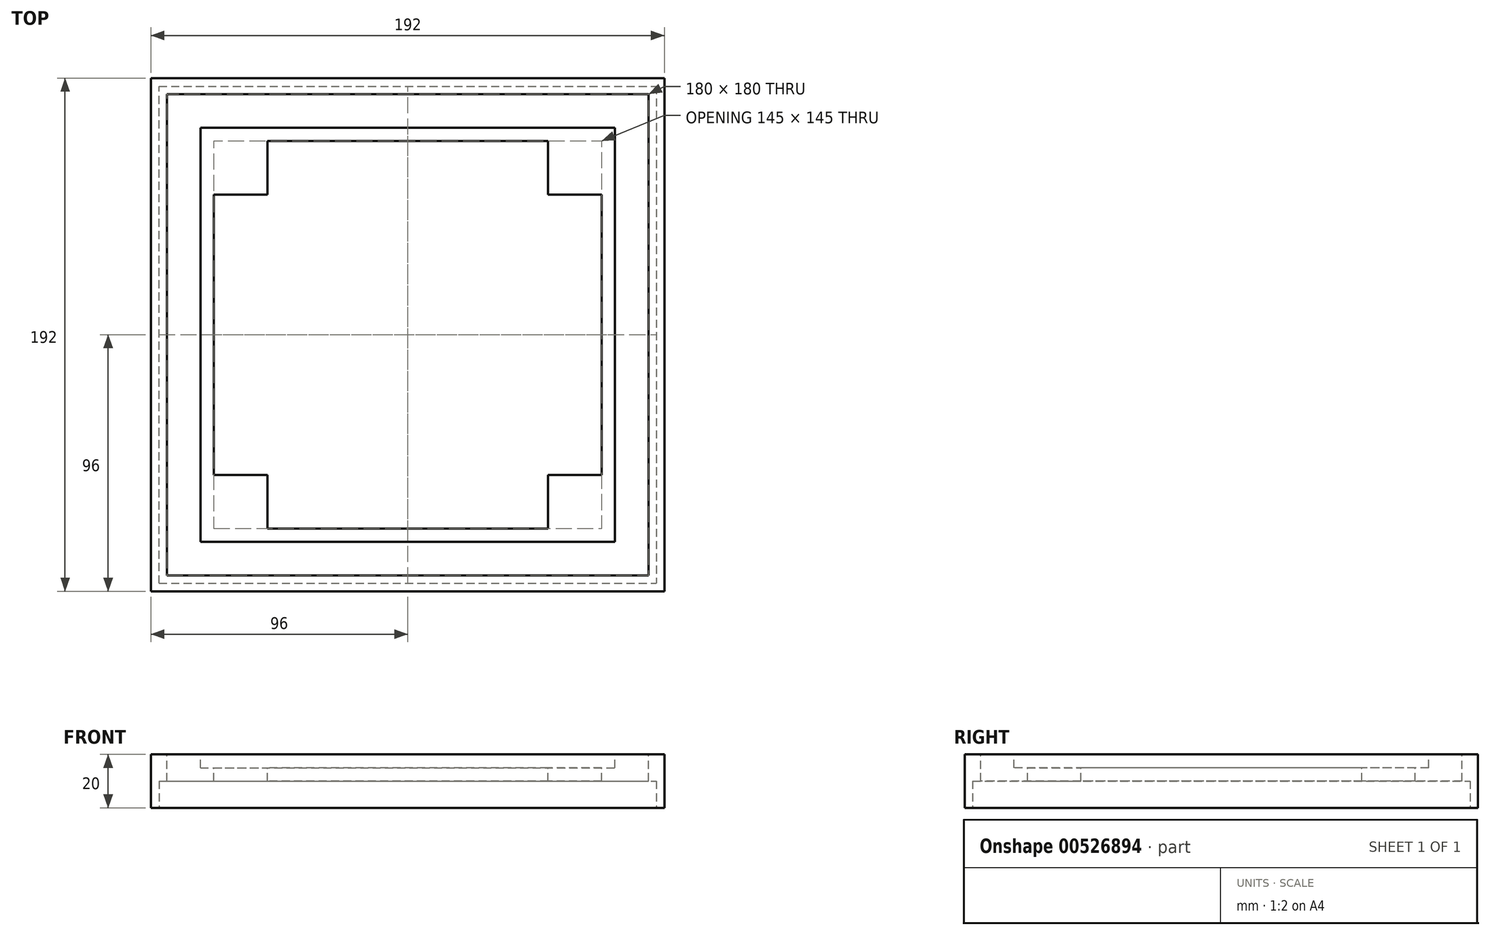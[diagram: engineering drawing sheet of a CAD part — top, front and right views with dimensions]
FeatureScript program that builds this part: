
annotation { "Feature Type Name" : "Feature", "Feature Type Description" : "" }
export const myFeature = defineFeature(function(context is Context, id is Id, definition is map)
    precondition{}
    {
        {
            var Q0;
            Q0=qCreatedBy(makeId("Top.planeOp"),FACE);
            var sketch = newSketch(context, id + "F0", { "sketchPlane" : qUnion([Q0])});
            skLineSegment(sketch, "E0.bottom", {"start": v(90, -90) * mm, "end": v(-90, -90) * mm});
            skLineSegment(sketch, "E0.top", {"start": v(90, 90) * mm, "end": v(-90, 90) * mm});
            skLineSegment(sketch, "E0.left", {"start": v(90, -90) * mm, "end": v(90, 90) * mm});
            skLineSegment(sketch, "E0.right", {"start": v(-90, -90) * mm, "end": v(-90, 90) * mm});
            skPoint(sketch, "E0.middle", {"position": v(0, 0) * mm});
            skSolve(sketch);
        }
        {
            var Q0;
            Q0=makeQuery(id+"F0.imprint","IMPRINT",FACE,{"disambiguationData":[TD([[makeQuery(id+"F0.imprint","IMPRINT",EDGE,{"derivedFrom":sQuery(id+"F0.wireOp",EDGE,"E0.bottom")}),-1.0]])]});
            extrude(context, id + "F1", {"entities" : qUnion([Q0]), "depth" : 70 * mm, "offsetDistance" : 25 * mm});
        }
        {
            var Q0;
            Q0=makeQuery(id+"F1.opExtrude","CAP_FACE",FACE,{"disambiguationData":[OSD([sQuery(id+"F0.wireOp",EDGE,"E0.bottom"),sQuery(id+"F0.wireOp",EDGE,"E0.top"),sQuery(id+"F0.wireOp",EDGE,"E0.left"),sQuery(id+"F0.wireOp",EDGE,"E0.right")])],"isStart":false});
            shell(context, id + "F2", {"entities" : qUnion([Q0]), "thickness" : 5 * mm});
        }
        {
            var Q0;
            Q0=makeQuery(id+"F1.opExtrude","CAP_FACE",FACE,{"disambiguationData":[OSD([sQuery(id+"F0.wireOp",EDGE,"E0.bottom"),sQuery(id+"F0.wireOp",EDGE,"E0.top"),sQuery(id+"F0.wireOp",EDGE,"E0.left"),sQuery(id+"F0.wireOp",EDGE,"E0.right")])],"isStart":false});
            var sketch = newSketch(context, id + "F3", { "sketchPlane" : qUnion([Q0])});
            skLineSegment(sketch, "E1.bottom", {"start": v(-85, 85) * mm, "end": v(85, 85) * mm});
            skLineSegment(sketch, "E1.top", {"start": v(-85, -85) * mm, "end": v(85, -85) * mm});
            skLineSegment(sketch, "E1.left", {"start": v(-85, 85) * mm, "end": v(-85, -85) * mm});
            skLineSegment(sketch, "E1.right", {"start": v(85, 85) * mm, "end": v(85, -85) * mm});
            skPoint(sketch, "E1.middle", {"position": v(0, 0) * mm});
            skSolve(sketch);
        }
        {
            var Q0;
            Q0=qSketchRegion(id+"F3",true);
            extrude(context, id + "F4", {"entities" : qUnion([Q0]), "operationType" : NewBodyOperationType.ADD, "oppositeDirection" : true, "depth" : 10 * mm, "offsetDistance" : 25 * mm});
        }
        {
            var Q0;
            Q0=makeQuery(id+"F4.boolean.opBoolean","MERGE",FACE,{"derivedFrom":[makeQuery(id+"F1.opExtrude","CAP_FACE",FACE,{"disambiguationData":[OSD([sQuery(id+"F0.wireOp",EDGE,"E0.bottom"),sQuery(id+"F0.wireOp",EDGE,"E0.top"),sQuery(id+"F0.wireOp",EDGE,"E0.left"),sQuery(id+"F0.wireOp",EDGE,"E0.right")])],"isStart":false}),makeQuery(id+"F4.opExtrude","CAP_FACE",FACE,{"disambiguationData":[OSD([sQuery(id+"F3.wireOp",EDGE,"E1.bottom"),sQuery(id+"F3.wireOp",EDGE,"E1.top"),sQuery(id+"F3.wireOp",EDGE,"E1.left"),sQuery(id+"F3.wireOp",EDGE,"E1.right")])],"isStart":true})]});
            var sketch = newSketch(context, id + "F5", { "sketchPlane" : qUnion([Q0])});
            skLineSegment(sketch, "E2.bottom", {"start": v(-77.5, 77.5) * mm, "end": v(77.5, 77.5) * mm});
            skLineSegment(sketch, "E2.top", {"start": v(-77.5, -77.5) * mm, "end": v(77.5, -77.5) * mm});
            skLineSegment(sketch, "E2.left", {"start": v(-77.5, 77.5) * mm, "end": v(-77.5, -77.5) * mm});
            skLineSegment(sketch, "E2.right", {"start": v(77.5, 77.5) * mm, "end": v(77.5, -77.5) * mm});
            skPoint(sketch, "E2.middle", {"position": v(0, 0) * mm});
            skSolve(sketch);
        }
        {
            var Q0;
            Q0=qSketchRegion(id+"F5",true);
            var Q1;
            Q1=makeQuery(id+"F5.imprint","IMPRINT",FACE,{"disambiguationData":[TD([[makeQuery(id+"F5.imprint","IMPRINT",EDGE,{"derivedFrom":sQuery(id+"F5.wireOp",EDGE,"E2.bottom")}),-1.0]])]});
            extrude(context, id + "F6", {"entities" : qUnion([Q0, Q1]), "operationType" : NewBodyOperationType.REMOVE, "oppositeDirection" : true, "depth" : 5 * mm, "offsetDistance" : 25 * mm});
        }
        {
            var Q0;
            Q0=makeQuery(id+"F6.boolean.opBoolean","COPY",FACE,{"derivedFrom":makeQuery(id+"F6.opExtrude","CAP_FACE",FACE,{"disambiguationData":[OSD([sQuery(id+"F5.wireOp",EDGE,"E2.bottom"),sQuery(id+"F5.wireOp",EDGE,"E2.top"),sQuery(id+"F5.wireOp",EDGE,"E2.left"),sQuery(id+"F5.wireOp",EDGE,"E2.right")])],"isStart":false})});
            var sketch = newSketch(context, id + "F7", { "sketchPlane" : qUnion([Q0])});
            skLineSegment(sketch, "E3.bottom", {"start": v(72.5, 72.5) * mm, "end": v(-72.5, 72.5) * mm});
            skLineSegment(sketch, "E3.top", {"start": v(72.5, -72.5) * mm, "end": v(-72.5, -72.5) * mm});
            skLineSegment(sketch, "E3.left", {"start": v(72.5, 72.5) * mm, "end": v(72.5, -72.5) * mm});
            skLineSegment(sketch, "E3.right", {"start": v(-72.5, 72.5) * mm, "end": v(-72.5, -72.5) * mm});
            skPoint(sketch, "E3.middle", {"position": v(0, 0) * mm});
            skSolve(sketch);
        }
        {
            var Q0;
            Q0=makeQuery(id+"F7.imprint","IMPRINT",FACE,{"disambiguationData":[TD([[makeQuery(id+"F7.imprint","IMPRINT",EDGE,{"derivedFrom":sQuery(id+"F7.wireOp",EDGE,"E3.bottom")}),1.0]])]});
            extrude(context, id + "F8", {"entities" : qUnion([Q0]), "operationType" : NewBodyOperationType.REMOVE, "oppositeDirection" : true, "depth" : 25 * mm, "offsetDistance" : 25 * mm});
        }
        {
            var Q0;
            Q0=makeQuery(id+"F6.boolean.opBoolean","COPY",FACE,{"derivedFrom":makeQuery(id+"F6.opExtrude","CAP_FACE",FACE,{"disambiguationData":[OSD([sQuery(id+"F5.wireOp",EDGE,"E2.bottom"),sQuery(id+"F5.wireOp",EDGE,"E2.top"),sQuery(id+"F5.wireOp",EDGE,"E2.left"),sQuery(id+"F5.wireOp",EDGE,"E2.right")])],"isStart":false})});
            var sketch = newSketch(context, id + "F9", { "sketchPlane" : qUnion([Q0])});
            skLineSegment(sketch, "E4.bottom", {"start": v(-72.5, 72.5) * mm, "end": v(-52.5, 72.5) * mm});
            skLineSegment(sketch, "E4.top", {"start": v(-72.5, 52.5) * mm, "end": v(-52.5, 52.5) * mm});
            skLineSegment(sketch, "E4.left", {"start": v(-72.5, 72.5) * mm, "end": v(-72.5, 52.5) * mm});
            skLineSegment(sketch, "E4.right", {"start": v(-52.5, 72.5) * mm, "end": v(-52.5, 52.5) * mm});
            skLineSegment(sketch, "E5.bottom", {"start": v(72.5, 72.5) * mm, "end": v(52.5, 72.5) * mm});
            skLineSegment(sketch, "E5.top", {"start": v(72.5, 52.5) * mm, "end": v(52.5, 52.5) * mm});
            skLineSegment(sketch, "E5.left", {"start": v(72.5, 72.5) * mm, "end": v(72.5, 52.5) * mm});
            skLineSegment(sketch, "E5.right", {"start": v(52.5, 72.5) * mm, "end": v(52.5, 52.5) * mm});
            skLineSegment(sketch, "E6.bottom", {"start": v(72.5, -72.5) * mm, "end": v(52.5, -72.5) * mm});
            skLineSegment(sketch, "E6.top", {"start": v(72.5, -52.5) * mm, "end": v(52.5, -52.5) * mm});
            skLineSegment(sketch, "E6.left", {"start": v(72.5, -72.5) * mm, "end": v(72.5, -52.5) * mm});
            skLineSegment(sketch, "E6.right", {"start": v(52.5, -72.5) * mm, "end": v(52.5, -52.5) * mm});
            skLineSegment(sketch, "E7.bottom", {"start": v(-72.5, -72.5) * mm, "end": v(-52.5, -72.5) * mm});
            skLineSegment(sketch, "E7.top", {"start": v(-72.5, -52.5) * mm, "end": v(-52.5, -52.5) * mm});
            skLineSegment(sketch, "E7.left", {"start": v(-72.5, -72.5) * mm, "end": v(-72.5, -52.5) * mm});
            skLineSegment(sketch, "E7.right", {"start": v(-52.5, -72.5) * mm, "end": v(-52.5, -52.5) * mm});
            skSolve(sketch);
        }
        {
            var Q0;
            Q0=makeQuery(id+"F9.imprint","IMPRINT",FACE,{"disambiguationData":[TD([[makeQuery(id+"F9.imprint","IMPRINT",EDGE,{"derivedFrom":sQuery(id+"F9.wireOp",EDGE,"E4.bottom")}),1.0]])]});
            var Q1;
            Q1=makeQuery(id+"F9.imprint","IMPRINT",FACE,{"disambiguationData":[TD([[makeQuery(id+"F9.imprint","IMPRINT",EDGE,{"derivedFrom":sQuery(id+"F9.wireOp",EDGE,"E5.bottom")}),1.0]])]});
            var Q2;
            Q2=makeQuery(id+"F9.imprint","IMPRINT",FACE,{"disambiguationData":[TD([[makeQuery(id+"F9.imprint","IMPRINT",EDGE,{"derivedFrom":sQuery(id+"F9.wireOp",EDGE,"E6.bottom")}),-1.0]])]});
            var Q3;
            Q3=makeQuery(id+"F9.imprint","IMPRINT",FACE,{"disambiguationData":[TD([[makeQuery(id+"F9.imprint","IMPRINT",EDGE,{"derivedFrom":sQuery(id+"F9.wireOp",EDGE,"E7.bottom")}),-1.0]])]});
            extrude(context, id + "F10", {"entities" : qUnion([Q0, Q1, Q2, Q3]), "operationType" : NewBodyOperationType.ADD, "oppositeDirection" : true, "depth" : 5 * mm, "offsetDistance" : 25 * mm});
        }
        {
            var Q0;
            Q0=makeQuery(id+"F1.opExtrude","CAP_FACE",FACE,{"disambiguationData":[OSD([sQuery(id+"F0.wireOp",EDGE,"E0.bottom"),sQuery(id+"F0.wireOp",EDGE,"E0.top"),sQuery(id+"F0.wireOp",EDGE,"E0.left"),sQuery(id+"F0.wireOp",EDGE,"E0.right")])],"isStart":true});
            var sketch = newSketch(context, id + "F11", { "sketchPlane" : qUnion([Q0])});
            skLineSegment(sketch, "E8.bottom", {"start": v(130.66, 148.52) * mm, "end": v(-106.26, 148.52) * mm});
            skLineSegment(sketch, "E8.top", {"start": v(130.66, -115.94) * mm, "end": v(-106.26, -115.94) * mm});
            skLineSegment(sketch, "E8.left", {"start": v(130.66, 148.52) * mm, "end": v(130.66, -115.94) * mm});
            skLineSegment(sketch, "E8.right", {"start": v(-106.26, 148.52) * mm, "end": v(-106.26, -115.94) * mm});
            skSolve(sketch);
        }
        {
            var Q0;
            Q0=makeQuery(id+"F11.imprint","IMPRINT",FACE,{"disambiguationData":[TD([[makeQuery(id+"F11.imprint","IMPRINT",EDGE,{"derivedFrom":sQuery(id+"F11.wireOp",EDGE,"E8.bottom")}),1.0]])]});
            extrude(context, id + "F12", {"entities" : qUnion([Q0]), "operationType" : NewBodyOperationType.REMOVE, "oppositeDirection" : true, "depth" : 25 * mm, "offsetDistance" : 25 * mm});
        }
        {
            var Q0;
            Q0=makeQuery(id+"F1.opExtrude","CAP_FACE",FACE,{"disambiguationData":[OSD([sQuery(id+"F0.wireOp",EDGE,"E0.bottom"),sQuery(id+"F0.wireOp",EDGE,"E0.top"),sQuery(id+"F0.wireOp",EDGE,"E0.left"),sQuery(id+"F0.wireOp",EDGE,"E0.right")])],"isStart":true});
            var sketch = newSketch(context, id + "F13", { "sketchPlane" : qUnion([Q0])});
            skLineSegment(sketch, "E9.bottom", {"start": v(99.38, 138.7) * mm, "end": v(-144.6, 138.7) * mm});
            skLineSegment(sketch, "E9.top", {"start": v(99.38, -180.9) * mm, "end": v(-144.6, -180.9) * mm});
            skLineSegment(sketch, "E9.left", {"start": v(99.38, 138.7) * mm, "end": v(99.38, -180.9) * mm});
            skLineSegment(sketch, "E9.right", {"start": v(-144.6, 138.7) * mm, "end": v(-144.6, -180.9) * mm});
            skSolve(sketch);
        }
        {
            var Q0;
            Q0=makeQuery(id+"F13.imprint","IMPRINT",FACE,{"disambiguationData":[TD([[makeQuery(id+"F13.imprint","IMPRINT",EDGE,{"derivedFrom":sQuery(id+"F13.wireOp",EDGE,"E9.bottom")}),1.0]])]});
            var Q1;
            Q1=makeQuery(id+"F13.imprint","IMPRINT",FACE,{"disambiguationData":[TD([[makeQuery(id+"F13.imprint","IMPRINT",EDGE,{"derivedFrom":makeQuery(id+"F1.opExtrude","CAP_EDGE",EDGE,{"disambiguationData":[OSD([sQuery(id+"F0.wireOp",EDGE,"E0.bottom")])],"isStart":true})}),1.0]])]});
            extrude(context, id + "F14", {"entities" : qUnion([Q0, Q1]), "operationType" : NewBodyOperationType.REMOVE, "oppositeDirection" : true, "depth" : 55 * mm, "offsetDistance" : 25 * mm, "hasSecondDirection" : true, "secondDirectionOppositeDirection" : false, "secondDirectionDepth" : 25 * mm});
        }
        {
            var Q0;
            Q0=makeQuery(id+"F10.boolean.opBoolean","MERGE",FACE,{"derivedFrom":[makeQuery(id+"F4.opExtrude","CAP_FACE",FACE,{"disambiguationData":[OSD([sQuery(id+"F3.wireOp",EDGE,"E1.bottom"),sQuery(id+"F3.wireOp",EDGE,"E1.top"),sQuery(id+"F3.wireOp",EDGE,"E1.left"),sQuery(id+"F3.wireOp",EDGE,"E1.right")])],"isStart":false}),makeQuery(id+"F10.opExtrude","CAP_FACE",FACE,{"disambiguationData":[OSD([sQuery(id+"F9.wireOp",EDGE,"E4.bottom"),sQuery(id+"F9.wireOp",EDGE,"E4.top"),sQuery(id+"F9.wireOp",EDGE,"E4.left"),sQuery(id+"F9.wireOp",EDGE,"E4.right")])],"isStart":false}),makeQuery(id+"F10.opExtrude","CAP_FACE",FACE,{"disambiguationData":[OSD([sQuery(id+"F9.wireOp",EDGE,"E5.bottom"),sQuery(id+"F9.wireOp",EDGE,"E5.top"),sQuery(id+"F9.wireOp",EDGE,"E5.left"),sQuery(id+"F9.wireOp",EDGE,"E5.right")])],"isStart":false}),makeQuery(id+"F10.opExtrude","CAP_FACE",FACE,{"disambiguationData":[OSD([sQuery(id+"F9.wireOp",EDGE,"E6.bottom"),sQuery(id+"F9.wireOp",EDGE,"E6.top"),sQuery(id+"F9.wireOp",EDGE,"E6.left"),sQuery(id+"F9.wireOp",EDGE,"E6.right")])],"isStart":false}),makeQuery(id+"F10.opExtrude","CAP_FACE",FACE,{"disambiguationData":[OSD([sQuery(id+"F9.wireOp",EDGE,"E7.bottom"),sQuery(id+"F9.wireOp",EDGE,"E7.top"),sQuery(id+"F9.wireOp",EDGE,"E7.left"),sQuery(id+"F9.wireOp",EDGE,"E7.right")])],"isStart":false})]});
            var sketch = newSketch(context, id + "F15", { "sketchPlane" : qUnion([Q0])});
            skLineSegment(sketch, "E10.bottom", {"start": v(-96, -96) * mm, "end": v(96, -96) * mm});
            skLineSegment(sketch, "E10.top", {"start": v(-96, 96) * mm, "end": v(96, 96) * mm});
            skLineSegment(sketch, "E10.left", {"start": v(-96, -96) * mm, "end": v(-96, 96) * mm});
            skLineSegment(sketch, "E10.right", {"start": v(96, -96) * mm, "end": v(96, 96) * mm});
            skPoint(sketch, "E10.middle", {"position": v(0, 0) * mm});
            skLineSegment(sketch, "E11.0", {"start": v(-90, -90) * mm, "end": v(90, -90) * mm});
            skLineSegment(sketch, "E12.0.0", {"start": v(90, -90) * mm, "end": v(90, 90) * mm});
            skLineSegment(sketch, "E12.0.1", {"start": v(90, 90) * mm, "end": v(-90, 90) * mm});
            skLineSegment(sketch, "E12.0.2", {"start": v(-90, 90) * mm, "end": v(-90, -90) * mm});
            skLineSegment(sketch, "E13.0", {"start": v(-90, 90) * mm, "end": v(90, 90) * mm});
            skSolve(sketch);
        }
        {
            var Q0;
            Q0=makeQuery(id+"F15.imprint","IMPRINT",FACE,{"disambiguationData":[TD([[makeQuery(id+"F15.imprint","IMPRINT",EDGE,{"derivedFrom":sQuery(id+"F15.wireOp",EDGE,"E10.bottom")}),1.0]])]});
            var Q1;
            Q1=makeQuery(id+"F4.boolean.opBoolean","MERGE",FACE,{"derivedFrom":[makeQuery(id+"F1.opExtrude","CAP_FACE",FACE,{"disambiguationData":[OSD([sQuery(id+"F0.wireOp",EDGE,"E0.bottom"),sQuery(id+"F0.wireOp",EDGE,"E0.top"),sQuery(id+"F0.wireOp",EDGE,"E0.left"),sQuery(id+"F0.wireOp",EDGE,"E0.right")])],"isStart":false}),makeQuery(id+"F4.opExtrude","CAP_FACE",FACE,{"disambiguationData":[OSD([sQuery(id+"F3.wireOp",EDGE,"E1.bottom"),sQuery(id+"F3.wireOp",EDGE,"E1.top"),sQuery(id+"F3.wireOp",EDGE,"E1.left"),sQuery(id+"F3.wireOp",EDGE,"E1.right")])],"isStart":true})]});
            extrude(context, id + "F16", {"entities" : qUnion([Q0]), "depth" : 10 * mm, "offsetDistance" : 25 * mm, "hasSecondDirection" : true, "secondDirectionBound" : SecondDirectionBoundingType.UP_TO_SURFACE, "secondDirectionOppositeDirection" : true, "secondDirectionDepth" : 25 * mm, "secondDirectionBoundEntityFace" : qUnion([Q1])});
        }
        {
            var Q0;
            Q0=makeQuery(id+"F14.boolean.opBoolean","COPY",FACE,{"derivedFrom":makeQuery(id+"F14.opExtrude","CAP_FACE",FACE,{"disambiguationData":[OSD([sQuery(id+"F13.wireOp",EDGE,"E9.bottom"),sQuery(id+"F13.wireOp",EDGE,"E9.top"),sQuery(id+"F13.wireOp",EDGE,"E9.left"),sQuery(id+"F13.wireOp",EDGE,"E9.right")])],"isStart":false})});
            var Q1;
            Q1=makeQuery(id+"F10.boolean.opBoolean","MERGE",FACE,{"derivedFrom":[makeQuery(id+"F4.opExtrude","CAP_FACE",FACE,{"disambiguationData":[OSD([sQuery(id+"F3.wireOp",EDGE,"E1.bottom"),sQuery(id+"F3.wireOp",EDGE,"E1.top"),sQuery(id+"F3.wireOp",EDGE,"E1.left"),sQuery(id+"F3.wireOp",EDGE,"E1.right")])],"isStart":false}),makeQuery(id+"F10.opExtrude","CAP_FACE",FACE,{"disambiguationData":[OSD([sQuery(id+"F9.wireOp",EDGE,"E4.bottom"),sQuery(id+"F9.wireOp",EDGE,"E4.top"),sQuery(id+"F9.wireOp",EDGE,"E4.left"),sQuery(id+"F9.wireOp",EDGE,"E4.right")])],"isStart":false}),makeQuery(id+"F10.opExtrude","CAP_FACE",FACE,{"disambiguationData":[OSD([sQuery(id+"F9.wireOp",EDGE,"E5.bottom"),sQuery(id+"F9.wireOp",EDGE,"E5.top"),sQuery(id+"F9.wireOp",EDGE,"E5.left"),sQuery(id+"F9.wireOp",EDGE,"E5.right")])],"isStart":false}),makeQuery(id+"F10.opExtrude","CAP_FACE",FACE,{"disambiguationData":[OSD([sQuery(id+"F9.wireOp",EDGE,"E6.bottom"),sQuery(id+"F9.wireOp",EDGE,"E6.top"),sQuery(id+"F9.wireOp",EDGE,"E6.left"),sQuery(id+"F9.wireOp",EDGE,"E6.right")])],"isStart":false}),makeQuery(id+"F10.opExtrude","CAP_FACE",FACE,{"disambiguationData":[OSD([sQuery(id+"F9.wireOp",EDGE,"E7.bottom"),sQuery(id+"F9.wireOp",EDGE,"E7.top"),sQuery(id+"F9.wireOp",EDGE,"E7.left"),sQuery(id+"F9.wireOp",EDGE,"E7.right")])],"isStart":false})]});
            extrude(context, id + "F17", {"entities" : qUnion([Q0]), "operationType" : NewBodyOperationType.REMOVE, "endBound" : BoundingType.UP_TO_SURFACE, "oppositeDirection" : true, "depth" : 25 * mm, "endBoundEntityFace" : qUnion([Q1]), "offsetDistance" : 25 * mm});
        }
        {
            var Q0;
            Q0=makeQuery(id+"F16.opExtrude","CAP_FACE",FACE,{"disambiguationData":[OSD([sQuery(id+"F15.wireOp",EDGE,"E10.bottom"),sQuery(id+"F15.wireOp",EDGE,"E10.top"),sQuery(id+"F15.wireOp",EDGE,"E10.left"),sQuery(id+"F15.wireOp",EDGE,"E10.right"),sQuery(id+"F15.wireOp",EDGE,"E12.0.0"),sQuery(id+"F15.wireOp",EDGE,"E12.0.2"),sQuery(id+"F15.wireOp",EDGE,"E11.0"),sQuery(id+"F15.wireOp",EDGE,"E13.0")])],"isStart":false});
            var sketch = newSketch(context, id + "F18", { "sketchPlane" : qUnion([Q0])});
            skLineSegment(sketch, "E14.0", {"start": v(-93, 93) * mm, "end": v(93, 93) * mm});
            skLineSegment(sketch, "E14.1", {"start": v(-93, 93) * mm, "end": v(-93, -93) * mm});
            skLineSegment(sketch, "E14.2", {"start": v(-93, -93) * mm, "end": v(93, -93) * mm});
            skLineSegment(sketch, "E14.3", {"start": v(93, -93) * mm, "end": v(93, 93) * mm});
            skSolve(sketch);
        }
        {
            var Q0;
            Q0=makeQuery(id+"F18.imprint","IMPRINT",FACE,{"disambiguationData":[TD([[makeQuery(id+"F18.imprint","IMPRINT",EDGE,{"derivedFrom":makeQuery(id+"F16.opExtrude","CAP_EDGE",EDGE,{"disambiguationData":[OSD([sQuery(id+"F15.wireOp",EDGE,"E12.0.0")])],"isStart":false})}),1.0]])]});
            var Q1;
            Q1=makeQuery(id+"F18.imprint","IMPRINT",FACE,{"disambiguationData":[TD([[makeQuery(id+"F18.imprint","IMPRINT",EDGE,{"derivedFrom":sQuery(id+"F18.wireOp",EDGE,"E14.0")}),-1.0]])]});
            var Q2;
            {var subQ0=sQuery(id+"F9.wireOp",EDGE,"E7.right");var subQ1=sQuery(id+"F9.wireOp",EDGE,"E7.left");var subQ2=sQuery(id+"F9.wireOp",EDGE,"E7.top");var subQ3=sQuery(id+"F9.wireOp",EDGE,"E7.bottom");var subQ4=sQuery(id+"F9.wireOp",EDGE,"E6.right");var subQ5=sQuery(id+"F9.wireOp",EDGE,"E6.left");var subQ6=sQuery(id+"F9.wireOp",EDGE,"E6.top");var subQ7=sQuery(id+"F9.wireOp",EDGE,"E6.bottom");var subQ8=sQuery(id+"F9.wireOp",EDGE,"E5.right");var subQ9=sQuery(id+"F9.wireOp",EDGE,"E5.left");var subQ10=sQuery(id+"F9.wireOp",EDGE,"E5.top");var subQ11=sQuery(id+"F9.wireOp",EDGE,"E5.bottom");var subQ12=sQuery(id+"F9.wireOp",EDGE,"E4.right");var subQ13=sQuery(id+"F9.wireOp",EDGE,"E4.left");var subQ14=sQuery(id+"F9.wireOp",EDGE,"E4.top");var subQ15=sQuery(id+"F9.wireOp",EDGE,"E4.bottom");var subQ16=sQuery(id+"F3.wireOp",EDGE,"E1.right");var subQ17=sQuery(id+"F3.wireOp",EDGE,"E1.left");var subQ18=sQuery(id+"F3.wireOp",EDGE,"E1.top");var subQ19=sQuery(id+"F3.wireOp",EDGE,"E1.bottom");Q2=makeQuery(id+"F17.boolean.opBoolean","MERGE",FACE,{"derivedFrom":[makeQuery(id+"F10.boolean.opBoolean","MERGE",FACE,{"derivedFrom":[makeQuery(id+"F4.opExtrude","CAP_FACE",FACE,{"disambiguationData":[OSD([subQ19,subQ18,subQ17,subQ16])],"isStart":false}),makeQuery(id+"F10.opExtrude","CAP_FACE",FACE,{"disambiguationData":[OSD([subQ15,subQ14,subQ13,subQ12])],"isStart":false}),makeQuery(id+"F10.opExtrude","CAP_FACE",FACE,{"disambiguationData":[OSD([subQ11,subQ10,subQ9,subQ8])],"isStart":false}),makeQuery(id+"F10.opExtrude","CAP_FACE",FACE,{"disambiguationData":[OSD([subQ7,subQ6,subQ5,subQ4])],"isStart":false}),makeQuery(id+"F10.opExtrude","CAP_FACE",FACE,{"disambiguationData":[OSD([subQ3,subQ2,subQ1,subQ0])],"isStart":false})]}),makeQuery(id+"F17.opExtrude","CAP_FACE",FACE,{"disambiguationData":[OSD([subQ19,subQ18,subQ17,subQ16,subQ15,subQ14,subQ13,subQ12,subQ11,subQ10,subQ9,subQ8,subQ7,subQ6,subQ5,subQ4,subQ3,subQ2,subQ1,subQ0])],"isStart":false})]});}
            extrude(context, id + "F19", {"entities" : qUnion([Q0, Q1]), "operationType" : NewBodyOperationType.REMOVE, "endBound" : BoundingType.UP_TO_SURFACE, "oppositeDirection" : true, "depth" : 25 * mm, "endBoundEntityFace" : qUnion([Q2]), "offsetDistance" : 25 * mm});
        }
    });
